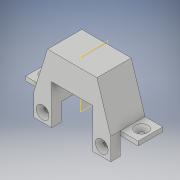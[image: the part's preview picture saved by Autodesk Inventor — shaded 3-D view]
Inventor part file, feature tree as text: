
AUTODESK INVENTOR PART (.ipt)
format: ipt  version: 2019 (Build 230136000, 136)  size: 355,840 bytes
history: native  units: mm
features: sketch x21, extrude x18, plane x3, mirror x2, chamfer x2, projected_geometry x2
ambient origin geometry x8: Origin, YZ Plane, XZ Plane, XY Plane, X Axis, Y Axis, Z Axis, Center Point
bodies: Solid1 (feature_tree)
feature tree (48):
  extrude  "Extrusion1"  Depth=10.6mm
  sketch  "Sketch2"  dims[d2=1.1mm d3=1.1mm]
  sketch  "Sketch3"  dims[d4=7.4mm d5=7.4mm]
  sketch  "Sketch4"  dims[d6=3.0mm d7=0.0mm d8=30.0mm]
  extrude  "Extrusion2"  Depth=1.1mm
  extrude  "Extrusion3"  Depth=7.4mm
  extrude  "Extrusion4"  Depth=30.0mm
  extrude  "Extrusion5"  Depth=3.0mm TaperAngle=0.0deg
  sketch  "Sketch7"  dims[d16=3.0mm d17=0.0mm d18=0.0mm d19=0.0mm]
  extrude  "Extrusion6"  Depth=16.0mm TaperAngle=0.0deg
  extrude  "Extrusion7"  TaperAngle=0.0deg  [1 undecoded]
  extrude  "Extrusion8"  Depth=18.0mm
  sketch  "Sketch12"  dims[d37=7.0mm d38=0.0mm d39=14.0mm d40=0.0mm]
  plane  "Work Plane1"
  mirror  "Mirror1"
  extrude  "Extrusion10"  Depth=14.0mm TaperAngle=0.0deg
  extrude  "Extrusion11"  Depth=30.0mm
  extrude  "Extrusion13"  Depth=14.0mm TaperAngle=0.0deg
  extrude  "Extrusion14"  Depth=13.0mm
  extrude  "Extrusion15"  Depth=13.0mm
  sketch  "Sketch19"  dims[d60=9.0mm d61=3.0mm d62=0.0mm]
  extrude  "Extrusion16"  Depth=7.0mm TaperAngle=0.0deg
  chamfer  "Chamfer3"  Distance=7.0mm
  extrude  "Extrusion17"  Depth=3.0mm TaperAngle=0.0deg
  extrude  "Extrusion18"  Depth=3.0mm TaperAngle=0.0deg
  extrude  "Extrusion19"  Depth=3.0mm TaperAngle=0.0deg
  chamfer  "Chamfer4"  Distance=3.0mm Angle=45.0deg
  extrude  "Extrusion20"  [1 undecoded]
  plane  "Work Plane2"
  mirror  "Mirror2"
  sketch  "Sketch1"  dims[d0=30.0mm d1=10.6mm]
  sketch  "Sketch5"  dims[d9=14.0mm d10=3.0mm d11=0.0mm]
  sketch  "Sketch6"  dims[d12=3.0mm d13=0.0mm d14=16.0mm d15=0.0mm]
  sketch  "Sketch8"  dims[d23=2000.0mm d24=0.0mm d25=18.0mm]
  sketch  "Sketch9"  dims[d26=3.0mm d27=14.0mm d28=0.0mm]
  projected_geometry  "Projected Loop1"
  sketch  "Sketch10"  dims[d35=-15.0mm d36=30.0mm]
  sketch  "Sketch13"  dims[d43=2.0mm d44=0.0mm d45=13.0mm]
  sketch  "Sketch14"  dims[d46=7.0mm d47=0.0mm d48=13.0mm]
  sketch  "Sketch16"  dims[d49=13.0mm d50=7.0mm d51=0.0mm]
  sketch  "Sketch17"  dims[d52=3.3mm d53=7.0mm d54=0.0mm]
  sketch  "Sketch18"  dims[d55=3.0mm d56=2.0mm d57=45.0deg d58=3.0mm d59=0.0mm]
  sketch  "Sketch20"  dims[d63=3.3mm d64=3.0mm d65=0.0mm d66=3.0mm d67=2.0mm d68=45.0deg]
  sketch  "Sketch21"  dims[d69=25.0mm d70=0.0mm d71=-18.0mm]
  sketch  "Sketch22"
  sketch  "Sketch24"
  projected_geometry  "Projected Loop3"
  plane  "Work Plane3"
note: 2 required parameter values undecoded (feature->parameter linkage not recoverable at this tier; creation-order binding heuristic only, values carry confidence <= 0.55)
